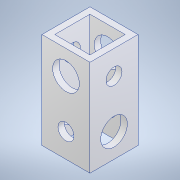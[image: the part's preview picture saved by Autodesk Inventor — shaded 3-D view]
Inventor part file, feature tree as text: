
AUTODESK INVENTOR PART (.ipt)
format: ipt  version: 2020.3 (Build 243373000, 373)  size: 150,016 bytes
history: native  units: mm
features: sketch x5, hole x4, other x1, extrude x1
ambient origin geometry x8: Origin, YZ Plane, XZ Plane, XY Plane, X Axis, Y Axis, Z Axis, Center Point
bodies: Body1 (feature_tree)
feature tree (11):
  other  "ソリッド1"
  extrude  "押し出し1"  Depth=9.0mm
  hole  "穴1"  [1 undecoded]
  hole  "穴2"  [1 undecoded]
  hole  "穴3"  [1 undecoded]
  hole  "穴4"  [1 undecoded]
  sketch  "スケッチ1"
  sketch  "スケッチ2"
  sketch  "スケッチ3"
  sketch  "スケッチ4"
  sketch  "スケッチ5"
note: 4 required parameter values undecoded (feature->parameter linkage not recoverable at this tier; creation-order binding heuristic only, values carry confidence <= 0.55)
